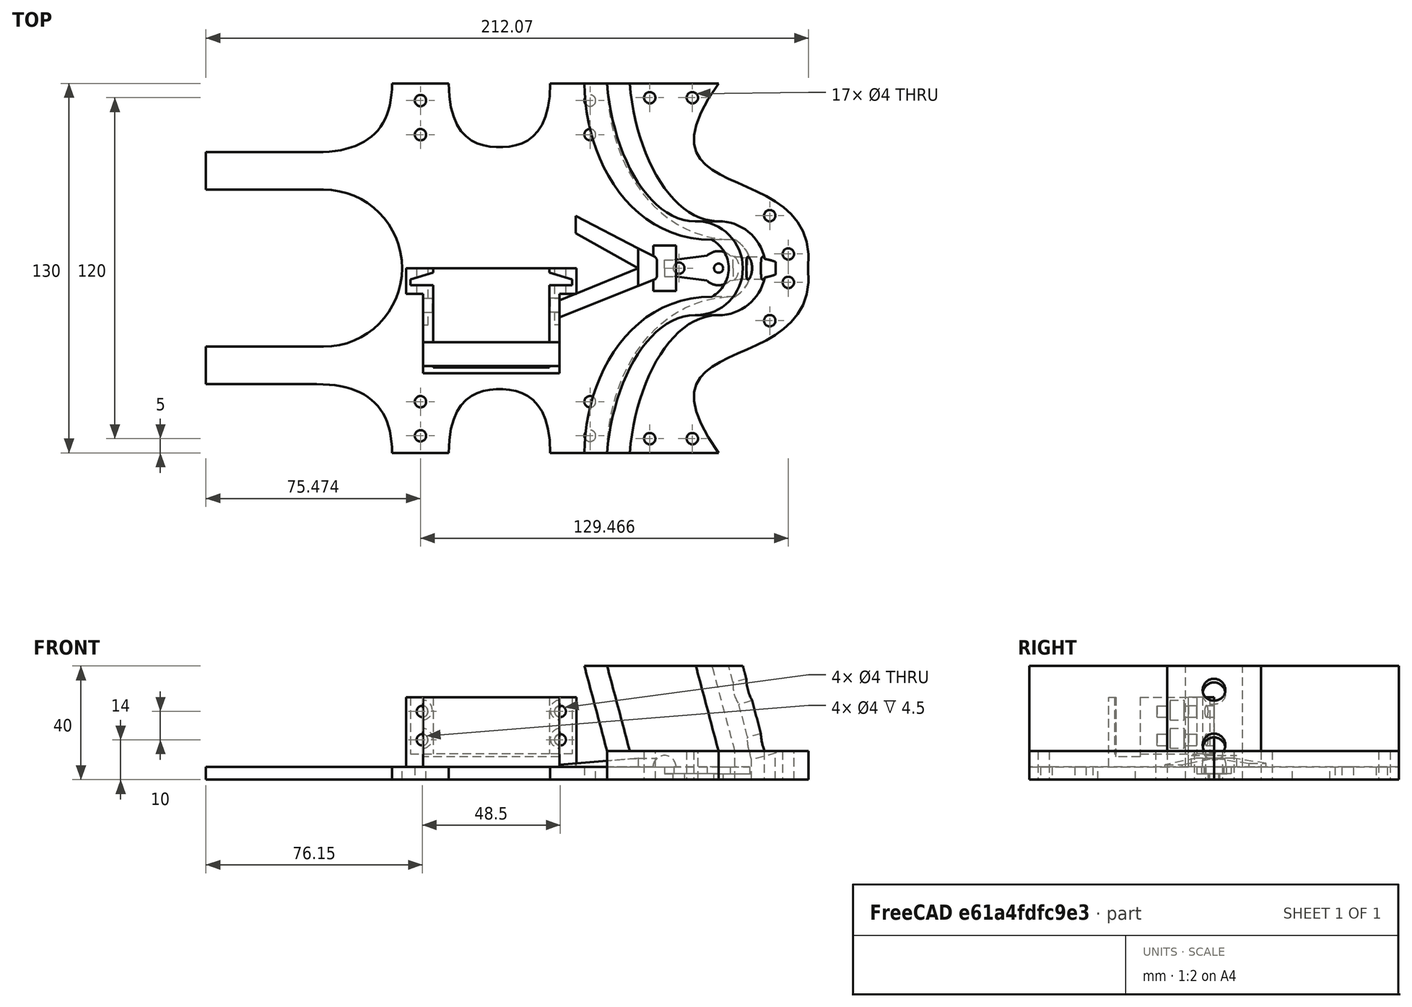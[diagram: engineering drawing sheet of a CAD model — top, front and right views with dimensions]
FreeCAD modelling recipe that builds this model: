
FCSTD DOCUMENT  (FreeCAD 0.18.4R)
Label: Crawler_bottom_2
License: All rights reserved
LicenseURL: http://en.wikipedia.org/wiki/All_rights_reserved
objects: TechDraw::DrawViewDimension×25, Sketcher::SketchObject×17, Part::Extrusion×6, PartDesign::Pocket×6, TechDraw::DrawViewPart×6, PartDesign::FeatureBase×3, PartDesign::Body×3, Part::Mirroring×3, Part::MultiFuse×3, Part::Fuse×3, Part::Cut×2, TechDraw::DrawSVGTemplate×2, TechDraw::DrawViewAnnotation×2, TechDraw::DrawPage×2, Spreadsheet::Sheet×1, PartDesign::Pad×1, Part::Loft×1
note: 55 computed .brp shape members not serialized (recipe doc carries the construction recipe); baked Part::Feature solids carry a one-line shape summary decoded from their .brp

FEATURE [Sketcher::SketchObject] Sketch
  expr: Constraints[11] = Constraints.dv
  expr: Constraints[5] = Constraints.dv
  expr: Constraints[10] = Constraints.dv
  expr: Constraints[4] = Constraints.dh
  expr: Constraints[3] = Constraints.diameterHole
  sketch-geometry (4):
    g0: Circle CenterX=-33 CenterY=5 CenterZ=0 NormalX=0 NormalY=0 NormalZ=1 AngleXU=0 Radius=4
    g1: Circle CenterX=-33 CenterY=-5 CenterZ=0 NormalX=0 NormalY=0 NormalZ=1 AngleXU=0 Radius=4
    g2: Circle CenterX=15 CenterY=5 CenterZ=0 NormalX=0 NormalY=0 NormalZ=1 AngleXU=0 Radius=4
    g3: Circle CenterX=15 CenterY=-5 CenterZ=0 NormalX=0 NormalY=0 NormalZ=1 AngleXU=0 Radius=4
  constraints (12):
    c: DistanceY(g-1,g0) = 5  'dv'
    c: Radius(g0) = 4  'diameterHole'
    c: DistanceX(g0,g-1) = 33  'dh'
    c: Radius(g1) = 4
    c: DistanceX(g1,g-1) = 33
    c: DistanceY(g1,g-1) = 5
    c: Equal(g0,g2) = 4  'diameterHole'
    c: Equal(g1,g3) = 4
    c: DistanceX(g-1,g2) = 15
    c: DistanceX(g-1,g3) = 15
    c: DistanceY(g3,g-1) = 5
    c: DistanceY(g-1,g2) = 5
FEATURE [Sketcher::SketchObject] Sketch001
  sketch-geometry (51):
    g0: GeomPoint X=-180.398 Y=40.8191 Z=0
    g1: LineSegment StartX=-180.398 StartY=40.8191 StartZ=0 EndX=-141.416 EndY=40.8191 EndZ=0
    g2: ArcOfCircle CenterX=0 CenterY=0 CenterZ=0 NormalX=0 NormalY=0 NormalZ=1 AngleXU=0 Radius=11.54 StartAngle=0 EndAngle=1.04825
    g3: ArcOfCircle CenterX=0 CenterY=0 CenterZ=0 NormalX=0 NormalY=0 NormalZ=1 AngleXU=0 Radius=1.6 StartAngle=0 EndAngle=3.14159
    g4: LineSegment StartX=1.6 StartY=0 StartZ=0 EndX=11.54 EndY=0 EndZ=0
    g5: LineSegment StartX=-1.6 StartY=2e-16 StartZ=0 EndX=-111.4 EndY=0 EndZ=0
    g6: ArcOfCircle CenterX=-139.032 CenterY=0 CenterZ=0 NormalX=0 NormalY=0 NormalZ=1 AngleXU=0 Radius=27.6319 StartAngle=0 EndAngle=1.5708
    g7: LineSegment StartX=-139.032 StartY=27.6319 StartZ=0 EndX=-180.398 EndY=27.6319 EndZ=0
    g8: LineSegment StartX=-180.398 StartY=27.6319 StartZ=0 EndX=-180.398 EndY=40.8191 EndZ=0
    g9: LineSegment [constr] StartX=-139.032 StartY=27.6319 StartZ=0 EndX=-139.032 EndY=0 EndZ=0
    g10: Circle [constr] CenterX=-141.416 CenterY=40.8191 CenterZ=0 NormalX=0 NormalY=0 NormalZ=1 AngleXU=0 Radius=2
    g11: Circle [constr] CenterX=-114.926 CenterY=40.8191 CenterZ=0 NormalX=0 NormalY=0 NormalZ=1 AngleXU=0 Radius=2
    g12: Circle [constr] CenterX=-114.926 CenterY=65 CenterZ=0 NormalX=0 NormalY=0 NormalZ=1 AngleXU=0 Radius=2
    g13: BSplineCurve PolesCount=3 KnotsCount=2 Degree=2 IsPeriodic=0
    g14: GeomPoint [constr] X=-141.416 Y=40.8191 Z=0
    g15: GeomPoint [constr] X=-114.926 Y=65 Z=0
    g16: LineSegment StartX=-114.926 StartY=65 StartZ=0 EndX=-94.9256 EndY=65 EndZ=0
    g17-g21: Circle [constr] x5 (B-spline internal-alignment scaffolding for g22; pole/knot coordinates omitted)
    g22: BSplineCurve PolesCount=5 KnotsCount=3 Degree=3 IsPeriodic=0
    g23: GeomPoint [constr] X=-94.9256 Y=65 Z=0
    g24: GeomPoint [constr] X=-77.0831 Y=42.5915 Z=0
    g25: GeomPoint [constr] X=-59.2405 Y=65 Z=0
    g26: LineSegment StartX=-59.2405 StartY=65 StartZ=0 EndX=-39.2405 EndY=65 EndZ=0
    g27-g30: Circle [constr] x4 (B-spline internal-alignment scaffolding for g31; pole/knot coordinates omitted)
    g31: BSplineCurve PolesCount=4 KnotsCount=2 Degree=3 IsPeriodic=0
    g32: GeomPoint [constr] X=-39.2405 Y=65 Z=0
    g33: GeomPoint [constr] X=5.75948 Y=10 Z=0
    g34: LineSegment [constr] StartX=-94.9256 StartY=46.3979 StartZ=0 EndX=-59.2405 EndY=46.3979 EndZ=0
    g35: LineSegment [constr] StartX=-94.9256 StartY=46.3979 StartZ=0 EndX=-77.0831 EndY=38.7852 EndZ=0
    g36: LineSegment [constr] StartX=-77.0831 StartY=38.7852 StartZ=0 EndX=-59.2405 EndY=46.3979 EndZ=0
    g37: LineSegment [constr] StartX=-141.416 StartY=40.8191 StartZ=0 EndX=-114.926 EndY=40.8191 EndZ=0
    g38: LineSegment [constr] StartX=-39.2405 StartY=65 StartZ=0 EndX=-39.2405 EndY=40 EndZ=0
    g39: LineSegment [constr] StartX=-39.2405 StartY=40 StartZ=0 EndX=-39.2405 EndY=10 EndZ=0
    g40: LineSegment [constr] StartX=-39.2405 StartY=10 StartZ=0 EndX=-24.2405 EndY=10 EndZ=0
    g41: LineSegment [constr] StartX=-59.2405 StartY=46.3979 StartZ=0 EndX=-59.2405 EndY=65 EndZ=0
    g42: LineSegment [constr] StartX=5.75948 StartY=10 StartZ=0 EndX=-24.2405 EndY=10 EndZ=0
    g43: LineSegment [constr] StartX=-114.926 StartY=40.8191 StartZ=0 EndX=-114.926 EndY=65 EndZ=0
    g44: LineSegment [constr] StartX=-94.9256 StartY=65 StartZ=0 EndX=-94.9256 EndY=46.3979 EndZ=0
    g45: Circle CenterX=-45.2405 CenterY=59 CenterZ=0 NormalX=0 NormalY=0 NormalZ=1 AngleXU=0 Radius=2
    g46: Circle CenterX=-45.2405 CenterY=47 CenterZ=0 NormalX=0 NormalY=0 NormalZ=1 AngleXU=0 Radius=2
    g47: LineSegment [constr] StartX=-45.2405 StartY=59 StartZ=0 EndX=-45.2405 EndY=47 EndZ=0
    g48: Circle CenterX=-104.926 CenterY=59 CenterZ=0 NormalX=0 NormalY=0 NormalZ=1 AngleXU=0 Radius=2
    g49: Circle CenterX=-104.926 CenterY=47 CenterZ=0 NormalX=0 NormalY=0 NormalZ=1 AngleXU=0 Radius=2
    g50: LineSegment [constr] StartX=-104.926 StartY=59 StartZ=0 EndX=-104.926 EndY=47 EndZ=0
  constraints (106):
    c: Coincident(g1,g0)
    c: Horizontal(g1)
    c: Coincident(g2,g-1)
    c: PointOnObject(g2,g-1)
    c: PointOnObject(g5,g-1)
    c: Coincident(g3,g-1)
    c: PointOnObject(g3,g-1)
    c: Coincident(g4,g3)
    c: Coincident(g4,g2)
    c: Horizontal(g4)
    c: Coincident(g5,g3)
    c: Radius(g3) = 1.6
    c: PointOnObject(g6,g-1)
    c: Coincident(g6,g5)
    c: Coincident(g7,g6)
    c: Horizontal(g7)
    c: Coincident(g8,g7)
    c: Vertical(g8)
    c: Coincident(g8,g0)
    c: Coincident(g9,g6)
    c: Vertical(g9)
    c: Coincident(g6,g9)
    c: Coincident(g13,g1)
    c: Radius(g10) = 2
    c: Equal(g10,g11)
    c: Equal(g10,g12)
    c: InternalAlignment(g10,g13)
    c: InternalAlignment(g11,g13)
    c: InternalAlignment(g12,g13)
    c: InternalAlignment(g14,g13)
    c: InternalAlignment(g15,g13)
    c: Coincident(g16,g13)
    c: Horizontal(g16)
    c: Coincident(g22,g16)
    c: Radius(g17) = 3
    c: Equal(g17, g18-g21) x4
    c: InternalAlignment(g17-g21 -> g22) x5
    c: InternalAlignment(g23,g22)
    c: InternalAlignment(g24,g22)
    c: InternalAlignment(g25,g22)
    c: Coincident(g26,g22)
    c: Horizontal(g26)
    c: Coincident(g31,g26)
    c: Radius(g27) = 5
    c: Equal(g27,g28)
    c: Equal(g27,g29)
    c: Equal(g27,g30)
    c: InternalAlignment(g27-g30 -> g31) x4
    c: InternalAlignment(g32,g31)
    c: InternalAlignment(g33,g31)
    c: Coincident(g34,g18)
    c: Coincident(g34,g20)
    c: Horizontal(g34)
    c: Coincident(g35,g18)
    c: Coincident(g35,g19)
    c: Coincident(g36,g20)
    c: Equal(g36,g35)
    c: Coincident(g19,g36)
    c: Coincident(g37,g1)
    c: Coincident(g37,g11)
    c: Horizontal(g37)
    c: Coincident(g38,g26)
    c: Coincident(g38,g28)
    c: Vertical(g38)
    c: Coincident(g39,g28)
    c: Vertical(g39)
    c: Coincident(g40,g39)
    c: Coincident(g40,g29)
    c: Horizontal(g40)
    c: DistanceY(g38,g38) = 25
    c: Coincident(g41,g20)
    c: Coincident(g41,g22)
    c: Vertical(g41)
    c: DistanceY(g39,g39) = 30
    c: Coincident(g42,g29)
    c: Horizontal(g42)
    c: DistanceX(g40,g40) = 15
    c: DistanceX(g42,g42) = 30
    c: Coincident(g43,g11)
    c: Coincident(g43,g13)
    c: Vertical(g43)
    c: Coincident(g44,g16)
    c: Coincident(g44,g18)
    c: Vertical(g44)
    c: Radius(g45) = 2
    c: Equal(g45,g46) = 2
    c: Coincident(g47,g45)
    c: Coincident(g47,g46)
    c: Vertical(g47)
    c: DistanceX(g26,g26) = 20
    c: DistanceX(g22,g45) = 14
    c: DistanceY(g45,g22) = 6
    c: DistanceY(g47,g47) = 12
    c: DistanceY(g2,g26) = 65
    c: Equal(g45,g48) = 2
    c: Equal(g48,g49) = 2
    c: Coincident(g50,g48)
    c: Coincident(g50,g49)
    c: Vertical(g50)
    c: Equal(g47,g50) = 12
    c: DistanceX(g16,g16) = 20
    c: DistanceX(g13,g48) = 10
    c: DistanceY(g48,g13) = 6
    c: DistanceY(g2,g16) = 65
    c: DistanceX(g2,g2) = 11.54
    c: DistanceY(g2,g2) = 10
FEATURE [Part::Extrusion] Extrude  label="arm"
  Base = -> Sketch001
  Dir = (0,0,1)
  DirMode = 2
  FaceMakerClass = Part::FaceMakerBullseye
  LengthFwd = 4.5
  LengthRev = 0
  Solid = true
  Symmetric = false
  expr: LengthFwd = global.height
FEATURE [Sketcher::SketchObject] Sketch003  label="ExtrudeToLayOn"
  AttachmentOffset = pos=(0,0,0) rot=(0,0,1;1.5708rad)
  MapMode = 2
  Placement = pos=(0,0,0) rot=(0,0,1;1.5708rad)
  Support = -> [Sketch001]
  expr: Constraints.length = Constraints.hi
  sketch-geometry (10):
    g0: LineSegment StartX=0 StartY=110 StartZ=0 EndX=0 EndY=50 EndZ=0
    g1: LineSegment StartX=-37 StartY=56 StartZ=0 EndX=-37 EndY=104 EndZ=0
    g2: LineSegment StartX=-37 StartY=104 StartZ=0 EndX=-9 EndY=104 EndZ=0
    g3: LineSegment StartX=-37 StartY=56 StartZ=0 EndX=-9 EndY=56 EndZ=0
    g4: LineSegment StartX=0 StartY=50 StartZ=0 EndX=-9 EndY=50 EndZ=0
    g5: LineSegment StartX=-9 StartY=50 StartZ=0 EndX=-9 EndY=56 EndZ=0
    g6: LineSegment StartX=0 StartY=110 StartZ=0 EndX=-9 EndY=110 EndZ=0
    g7: LineSegment StartX=-9 StartY=104 StartZ=0 EndX=-9 EndY=110 EndZ=0
    g8: LineSegment [constr] StartX=-9 StartY=104 StartZ=0 EndX=-9 EndY=80 EndZ=0
    g9: LineSegment [constr] StartX=-9 StartY=80 StartZ=0 EndX=-9 EndY=56 EndZ=0
  constraints (29):
    c: Vertical(g0)
    c: Vertical(g1)
    c: DistanceY(g0,g0) = 60
    c: Coincident(g2,g1)
    c: Horizontal(g2)
    c: DistanceX(g2,g2) = 28  'hi'
    c: Coincident(g3,g1)
    c: Horizontal(g3)
    c: DistanceX(g3,g3) = 28  'length'
    c: Coincident(g4,g0)
    c: Horizontal(g4)
    c: Coincident(g5,g4)
    c: Coincident(g5,g3)
    c: Vertical(g5)
    c: Coincident(g6,g0)
    c: Horizontal(g6)
    c: Vertical(g7)
    c: Coincident(g7,g6)
    c: Coincident(g2,g7)
    c: Equal(g5,g7)
    c: DistanceY(g1,g1) = 48
    c: DistanceX(g4,g0) = 9
    c: DistanceX(g1,g-1) = 37
    c: Coincident(g8,g2)
    c: Vertical(g8)
    c: Coincident(g9,g8)
    c: Coincident(g9,g3)
    c: Equal(g8,g9)
    c: DistanceY(g-1,g8) = 80
FEATURE [Part::Extrusion] Extrude001
  Base = -> Sketch003
  Dir = (0,0,1)
  DirMode = 2
  FaceMakerClass = Part::FaceMakerBullseye
  LengthFwd = 25
  LengthRev = 0
  Placement = pos=(0,0,2) rot=(0,0,1;0rad)
  Solid = true
  Symmetric = false
FEATURE [Sketcher::SketchObject] Sketch004  label="Servo"
  AttachmentOffset = pos=(0,-3,-2) rot=(0,0,1;0rad)
  MapMode = 5
  Placement = pos=(0,-3,25) rot=(0,0,1;0rad)
  Support = -> [Extrude001]
  expr: Constraints[35] = Constraints.strebeH
  sketch-geometry (21):
    g0: LineSegment StartX=-100.5 StartY=4.5 StartZ=0 EndX=-59.5 EndY=4.5 EndZ=0
    g1: LineSegment StartX=-59.5 StartY=-32 StartZ=0 EndX=-100.5 EndY=-32 EndZ=0
    g2: LineSegment [constr] StartX=-59.5 StartY=4.5 StartZ=0 EndX=-59.5 EndY=-1 EndZ=0
    g3: LineSegment [constr] StartX=-59.5 StartY=-1 StartZ=0 EndX=-51.5 EndY=-1 EndZ=0
    g4: LineSegment StartX=-51.5 StartY=-1 StartZ=0 EndX=-51.5 EndY=-3 EndZ=0
    g5: LineSegment StartX=-51.5 StartY=-3 StartZ=0 EndX=-59.5 EndY=-3 EndZ=0
    g6: LineSegment [constr] StartX=-100.5 StartY=4.5 StartZ=0 EndX=-100.5 EndY=-1 EndZ=0
    g7: LineSegment [constr] StartX=-100.5 StartY=-1 StartZ=0 EndX=-108.5 EndY=-1 EndZ=0
    g8: LineSegment StartX=-108.5 StartY=-1 StartZ=0 EndX=-108.5 EndY=-3 EndZ=0
    g9: LineSegment StartX=-108.5 StartY=-3 StartZ=0 EndX=-100.5 EndY=-3 EndZ=0
    g10: GeomPoint X=-80 Y=-3 Z=0
    g11: LineSegment [constr] StartX=-100.5 StartY=-3 StartZ=0 EndX=-80 EndY=-3 EndZ=0
    g12: LineSegment [constr] StartX=-80 StartY=-3 StartZ=0 EndX=-59.5 EndY=-3 EndZ=0
    g13: GeomPoint X=-59.5 Y=1.5 Z=0
    g14: GeomPoint X=-100.5 Y=1.5 Z=0
    g15: LineSegment StartX=-108.5 StartY=-1 StartZ=0 EndX=-100.5 EndY=1.5 EndZ=0
    g16: LineSegment StartX=-100.5 StartY=1.5 StartZ=0 EndX=-100.5 EndY=4.5 EndZ=0
    g17: LineSegment StartX=-51.5 StartY=-1 StartZ=0 EndX=-59.5 EndY=1.5 EndZ=0
    g18: LineSegment StartX=-59.5 StartY=1.5 StartZ=0 EndX=-59.5 EndY=4.5 EndZ=0
    g19: LineSegment StartX=-100.5 StartY=-3 StartZ=0 EndX=-100.5 EndY=-32 EndZ=0
    g20: LineSegment StartX=-59.5 StartY=-32 StartZ=0 EndX=-59.5 EndY=-3 EndZ=0
  constraints (54):
    c: Horizontal(g0)
    c: DistanceX(g0,g0) = 41  'vl'
    c: DistanceY(g1,g0) = 36.5
    c: Coincident(g2,g0)
    c: Vertical(g2)
    c: DistanceY(g2,g2) = 5.5  'vh'
    c: Coincident(g3,g2)
    c: Horizontal(g3)
    c: Coincident(g4,g3)
    c: Vertical(g4)
    c: Coincident(g5,g4)
    c: Horizontal(g5)
    c: DistanceX(g0,g1) = 0
    c: Vertical(g6)
    c: Coincident(g7,g6)
    c: Horizontal(g7)
    c: Coincident(g8,g7)
    c: Vertical(g8)
    c: Coincident(g9,g8)
    c: Horizontal(g9)
    c: Coincident(g6,g0)
    c: DistanceY(g6,g6) = 5.5
    c: DistanceY(g1,g9) = 29
    c: Horizontal(g1)
    c: DistanceX(g1,g1) = 41
    c: DistanceX(g7,g6) = 8
    c: DistanceX(g2,g3) = 8
    c: Coincident(g11,g10)
    c: Horizontal(g11)
    c: Coincident(g12,g10)
    c: Equal(g11,g12)
    c: DistanceX(g10,g-1) = 80  'HvonOrg'
    c: PointOnObject(g13,g2)
    c: DistanceY(g2,g13) = 2.5  'strebeH'
    c: PointOnObject(g14,g6)
    c: DistanceY(g6,g14) = 2.5
    c: Coincident(g15,g7)
    c: Coincident(g15,g14)
    c: Coincident(g16,g14)
    c: Coincident(g16,g0)
    c: Coincident(g17,g3)
    c: Coincident(g17,g13)
    c: Coincident(g18,g13)
    c: Coincident(g18,g0)
    c: Coincident(g19,g9)
    c: Coincident(g19,g1)
    c: Vertical(g19)
    c: Coincident(g20,g1)
    c: Vertical(g20)
    c: Coincident(g5,g20)
    c: Coincident(g5,g12)
    c: Coincident(g9,g11)
    c: Horizontal(g12)
    c: DistanceY(g1,g-1) = 32
FEATURE [PartDesign::FeatureBase] BaseFeature001
  BaseFeature = -> Extrude001
FEATURE [PartDesign::Pocket] Pocket001
  BaseFeature = -> BaseFeature001
  Length = 20
  Length2 = 100
  Profile = -> Sketch004
  Type = 0
FEATURE [Sketcher::SketchObject] Sketch005  label="ServoHoles"
  MapMode = 5
  Placement = pos=(0,2e-16,0) rot=(0,0.707107,0.707107;3.14159rad)
  Support = -> [Pocket001]
  expr: Constraints.height = 5mm + 5mm
  expr: Constraints[14] = Sketch004.Constraints.HvonOrg
  sketch-geometry (7):
    g0: Circle CenterX=55.75 CenterY=20 CenterZ=0 NormalX=0 NormalY=0 NormalZ=1 AngleXU=0 Radius=2
    g1: Circle CenterX=55.75 CenterY=10 CenterZ=0 NormalX=0 NormalY=0 NormalZ=1 AngleXU=0 Radius=2
    g2: Circle CenterX=104.25 CenterY=10 CenterZ=0 NormalX=0 NormalY=0 NormalZ=1 AngleXU=0 Radius=2
    g3: Circle CenterX=104.25 CenterY=20 CenterZ=0 NormalX=0 NormalY=0 NormalZ=1 AngleXU=0 Radius=2
    g4: GeomPoint X=57.75 Y=20 Z=0
    g5: GeomPoint X=102.25 Y=20 Z=0
    g6: GeomPoint X=80 Y=8 Z=0
  constraints (17):
    c: Radius(g0) = 2  'rad'
    c: Equal(g0,g1) = 2  'rad'
    c: DistanceY(g1,g0) = 10
    c: DistanceX(g0,g1) = 0
    c: Equal(g0,g3) = 2  'rad'
    c: Equal(g3,g2) = 2  'rad'
    c: DistanceY(g2,g3) = 10
    c: DistanceX(g3,g2) = 0
    c: DistanceY(g0,g3) = 0
    c: DistanceY(g-1,g1) = 10  'height'
    c: PointOnObject(g4,g0)
    c: PointOnObject(g5,g3)
    c: DistanceY(g4,g0) = 0
    c: DistanceY(g5,g4) = 0
    c: DistanceX(g-1,g6) = 80
    c: DistanceX(g4,g6) = 22.25
    c: DistanceX(g6,g5) = 22.25
FEATURE [PartDesign::Pocket] Pocket002
  BaseFeature = -> Pocket001
  Length = 20
  Length2 = 100
  Profile = -> Sketch005
  Type = 0
FEATURE [PartDesign::Body] Body001
  BaseFeature = -> Extrude001
  Group = -> [BaseFeature001,Sketch004,Pocket001,Sketch005,Pocket002]
  Origin = -> Origin001
  Placement = pos=(0,0,4) rot=(0,0,1;0rad)
  Tip = -> Pocket002
  expr: Placement.Base.y = global.offestSev
FEATURE [Sketcher::SketchObject] Sketch007
  Placement = pos=(2,0,17) rot=(0,0,1;1.5708rad)
  expr: Constraints[28] = Constraints.vh
  expr: Constraints[29] = Constraints.vh2
  sketch-geometry (12):
    g0: LineSegment StartX=1.28047 StartY=41.4016 StartZ=0 EndX=42.2805 EndY=41.4016 EndZ=0
    g1: LineSegment StartX=42.2805 StartY=4.90163 StartZ=0 EndX=1.04145 EndY=4.90163 EndZ=0
    g2: LineSegment StartX=42.2805 StartY=4.90163 StartZ=0 EndX=42.2805 EndY=31.3016 EndZ=0
    g3: LineSegment StartX=42.2805 StartY=41.4016 StartZ=0 EndX=42.2805 EndY=35.4016 EndZ=0
    g4: LineSegment StartX=42.2805 StartY=35.4016 StartZ=0 EndX=48.9967 EndY=35.4016 EndZ=0
    g5: LineSegment StartX=48.9967 StartY=35.4016 StartZ=0 EndX=48.9967 EndY=31.3016 EndZ=0
    g6: LineSegment StartX=48.9967 StartY=31.3016 StartZ=0 EndX=42.2805 EndY=31.3016 EndZ=0
    g7: LineSegment StartX=1.04145 StartY=4.90163 StartZ=0 EndX=1.04145 EndY=31.3016 EndZ=0
    g8: LineSegment StartX=1.28047 StartY=41.4016 StartZ=0 EndX=1.28047 EndY=35.4016 EndZ=0
    g9: LineSegment StartX=1.28047 StartY=35.4016 StartZ=0 EndX=-5.63119 EndY=35.4016 EndZ=0
    g10: LineSegment StartX=-5.63119 StartY=35.4016 StartZ=0 EndX=-5.63119 EndY=31.3016 EndZ=0
    g11: LineSegment StartX=-5.63119 StartY=31.3016 StartZ=0 EndX=1.04145 EndY=31.3016 EndZ=0
  constraints (31):
    c: Horizontal(g0)
    c: DistanceX(g0,g0) = 41  'v'
    c: DistanceY(g1,g0) = 36.5
    c: Coincident(g2,g1)
    c: Vertical(g2)
    c: DistanceY(g2,g2) = 26.4  'vh2'
    c: Coincident(g3,g0)
    c: Vertical(g3)
    c: DistanceY(g3,g3) = 6  'vh'
    c: Coincident(g4,g3)
    c: Horizontal(g4)
    c: Coincident(g5,g4)
    c: Vertical(g5)
    c: Coincident(g6,g5)
    c: Coincident(g6,g2)
    c: Horizontal(g6)
    c: DistanceX(g0,g1) = 0
    c: Vertical(g7)
    c: Vertical(g8)
    c: Coincident(g9,g8)
    c: Horizontal(g9)
    c: Coincident(g10,g9)
    c: Vertical(g10)
    c: Coincident(g11,g10)
    c: Coincident(g11,g7)
    c: Horizontal(g11)
    c: Coincident(g8,g0)
    c: Coincident(g1,g7)
    c: DistanceY(g8,g8) = 6
    c: DistanceY(g7,g7) = 26.4
    c: Horizontal(g1)
FEATURE [Sketcher::SketchObject] Sketch008  label="ServoHole"
  AttachmentOffset = pos=(0,0,4.5) rot=(0,0,1;0rad)
  Placement = pos=(0,0,4.5) rot=(0,0,1;1.5708rad)
  expr: AttachmentOffset.Base.z = global.height
  sketch-geometry (7):
    g0: GeomPoint X=0 Y=19 Z=0
    g1: LineSegment StartX=0 StartY=19 StartZ=0 EndX=2.9 EndY=19 EndZ=0
    g2: LineSegment StartX=2.9 StartY=19 StartZ=0 EndX=2.9 EndY=15.6827 EndZ=0
    g3: ArcOfCircle CenterX=0 CenterY=0 CenterZ=0 NormalX=0 NormalY=0 NormalZ=1 AngleXU=0 Radius=6 StartAngle=0 EndAngle=0.747584
    g4: LineSegment StartX=4.4 StartY=4.07922 StartZ=0 EndX=2.9 EndY=15.6827 EndZ=0
    g5: LineSegment StartX=0 StartY=0 StartZ=0 EndX=6 EndY=0 EndZ=0
    g6: LineSegment StartX=0 StartY=0 StartZ=0 EndX=0 EndY=19 EndZ=0
  constraints (18):
    c: PointOnObject(g0,g-2)
    c: DistanceY(g-1,g0) = 19  'servHoleL'
    c: Coincident(g1,g0)
    c: Horizontal(g1)
    c: DistanceX(g1,g1) = 2.9
    c: Coincident(g2,g1)
    c: Vertical(g2)
    c: Coincident(g3,g-1)
    c: Radius(g3) = 6
    c: PointOnObject(g3,g-1)
    c: DistanceX(g-1,g3) = 4.4
    c: Coincident(g4,g2)
    c: Distance(g4) = 11.7
    c: Coincident(g4,g3)
    c: Coincident(g5,g-1)
    c: Coincident(g5,g3)
    c: Coincident(g6,g-1)
    c: Coincident(g6,g0)
FEATURE [Spreadsheet::Sheet] Spreadsheet  label="global"
  cells = A1=height; B1(height)=4.5; A2=offsetBackwardServo; B2(offestSev)=0
FEATURE [Part::Extrusion] Extrude004
  Base = -> Sketch008
  Dir = (0,0,1)
  DirMode = 2
  FaceMakerClass = Part::FaceMakerBullseye
  LengthFwd = 2.45
  LengthRev = 0
  Reversed = true
  Solid = true
  Symmetric = false
FEATURE [Part::Mirroring] Part__Mirroring002  label="Extrude004 (Mirror #3)"
  Base = (0,0,0)
  Normal = (1,0,0)
  Source = -> Extrude004
FEATURE [Part::MultiFuse] Fusion003
  Shapes = -> [Part__Mirroring002,Extrude004]
FEATURE [Part::Cut] Cut
  Base = -> Extrude
  Tool = -> Fusion003
FEATURE [Part::Mirroring] Part__Mirroring  label="Extrude (Mirror #1)"
  Base = (0,0,0)
  Normal = (0,1,0)
  Source = -> Cut
FEATURE [Sketcher::SketchObject] Sketch009  label="servoScrewSmallWhole"
  Placement = pos=(0,0,4.5) rot=(0,0,1;0rad)
  expr: Placement.Base.z = global.height
  sketch-geometry (3):
    g0: GeomPoint X=-19 Y=0 Z=0
    g1: GeomPoint X=-14 Y=0 Z=0
    g2: Circle CenterX=-14 CenterY=0 CenterZ=0 NormalX=0 NormalY=0 NormalZ=1 AngleXU=0 Radius=2
  constraints (5):
    c: PointOnObject(g0,g-1)
    c: DistanceX(g0,g-1) = 19
    c: PointOnObject(g1,g-1)
    c: DistanceX(g0,g1) = 5
    c: Radius(g2) = 2
FEATURE [Sketcher::SketchObject] Sketch010  label="ServoHoles001"
  AttachmentOffset = pos=(0,0,-10.5) rot=(0,0,1;0rad)
  MapMode = 5
  Placement = pos=(-2.3e-15,-10.5,2.3e-15) rot=(0,0.707107,0.707107;3.14159rad)
  Support = -> [Pocket001]
  expr: Constraints.height = 5mm + 5mm + 4.5mm
  expr: Constraints[16] = Constraints.widthDist
  expr: Constraints[14] = Sketch004.Constraints.HvonOrg
  sketch-geometry (7):
    g0: Circle CenterX=55.75 CenterY=24.5 CenterZ=0 NormalX=0 NormalY=0 NormalZ=1 AngleXU=0 Radius=3.5
    g1: Circle CenterX=55.75 CenterY=14.5 CenterZ=0 NormalX=0 NormalY=0 NormalZ=1 AngleXU=0 Radius=3.5
    g2: Circle CenterX=104.25 CenterY=14.5 CenterZ=0 NormalX=0 NormalY=0 NormalZ=1 AngleXU=0 Radius=3.5
    g3: Circle CenterX=104.25 CenterY=24.5 CenterZ=0 NormalX=0 NormalY=0 NormalZ=1 AngleXU=0 Radius=3.5
    g4: GeomPoint X=59.25 Y=24.5 Z=0
    g5: GeomPoint X=100.75 Y=24.5 Z=0
    g6: GeomPoint X=80 Y=8 Z=0
  constraints (17):
    c: Radius(g0) = 3.5  'rad'
    c: Equal(g0,g1) = 2  'rad'
    c: DistanceY(g1,g0) = 10
    c: DistanceX(g0,g1) = 0
    c: Equal(g0,g3) = 2  'rad'
    c: Equal(g3,g2) = 2  'rad'
    c: DistanceY(g2,g3) = 10
    c: DistanceX(g3,g2) = 0
    c: DistanceY(g0,g3) = 0
    c: DistanceY(g-1,g1) = 14.5  'height'
    c: PointOnObject(g4,g0)
    c: PointOnObject(g5,g3)
    c: DistanceY(g4,g0) = 0
    c: DistanceY(g5,g4) = 0
    c: DistanceX(g-1,g6) = 80
    c: DistanceX(g4,g6) = 20.75  'widthDist'
    c: DistanceX(g6,g5) = 20.75
FEATURE [Sketcher::SketchObject] Sketch011  label="CableHole"
  MapMode = 5
  Placement = pos=(-56,1.23e-14,0) rot=(0.57735,0.57735,0.57735;2.0944rad)
  Support = -> [Pocket002]
  sketch-geometry (5):
    g0: GeomPoint X=-5 Y=4 Z=0
    g1: LineSegment StartX=-34.5 StartY=37.056 StartZ=0 EndX=-26 EndY=37.056 EndZ=0
    g2: LineSegment StartX=-26 StartY=37.056 StartZ=0 EndX=-26 EndY=8 EndZ=0
    g3: LineSegment StartX=-26 StartY=8 StartZ=0 EndX=-34.5 EndY=8 EndZ=0
    g4: LineSegment StartX=-34.5 StartY=8 StartZ=0 EndX=-34.5 EndY=37.056 EndZ=0
  constraints (13):
    c: DistanceX(g-1,g0) = -5
    c: Coincident(g1,g2)
    c: Coincident(g2,g3)
    c: Coincident(g3,g4)
    c: Coincident(g4,g1)
    c: Horizontal(g1)
    c: Horizontal(g3)
    c: Vertical(g2)
    c: Vertical(g4)
    c: DistanceX(g2,g0) = 21
    c: DistanceX(g3,g3) = 8.5
    c: DistanceY(g-1,g0) = 4
    c: DistanceY(g0,g2) = 4
FEATURE [Sketcher::SketchObject] Sketch013
  MapMode = 5
  Placement = pos=(0,0,0) rot=(1,0,0;1.5708rad)
  sketch-geometry (3):
    g0: LineSegment StartX=-59 StartY=5 StartZ=0 EndX=-22.1184 EndY=8 EndZ=0
    g1: LineSegment StartX=-22.1184 StartY=8 StartZ=0 EndX=-59 EndY=8 EndZ=0
    g2: LineSegment StartX=-59 StartY=8 StartZ=0 EndX=-59 EndY=5 EndZ=0
  constraints (8):
    c: Coincident(g1,g0)
    c: Horizontal(g1)
    c: Coincident(g2,g1)
    c: Coincident(g2,g0)
    c: Vertical(g2)
    c: DistanceX(g0,g-1) = 59
    c: DistanceY(g-1,g0) = 8
    c: DistanceY(g0,g1) = 3
FEATURE [Part::Extrusion] Extrude006
  Base = -> Sketch013
  Dir = (0,-1,2e-16)
  DirMode = 2
  FaceMakerClass = Part::FaceMakerBullseye
  LengthFwd = 30
  LengthRev = 30
  Solid = true
  Symmetric = false
FEATURE [Part::Fuse] Fusion
  Base = -> Cut
  Tool = -> Part__Mirroring
FEATURE [Part::Fuse] Fusion001
  Base = -> Fusion
  Tool = -> Body001
FEATURE [PartDesign::FeatureBase] BaseFeature002
  BaseFeature = -> Fusion001
FEATURE [PartDesign::Pocket] Pocket003
  BaseFeature = -> BaseFeature002
  Length = 10
  Length2 = 100
  Profile = -> Sketch009
  Type = 0
FEATURE [PartDesign::Pocket] Pocket
  BaseFeature = -> Pocket003
  Length = 5
  Length2 = 100
  Profile = -> Sketch010
  Type = 0
FEATURE [PartDesign::Pocket] Pocket004
  BaseFeature = -> Pocket
  Length = 50
  Length2 = 100
  Profile = -> Sketch011
  Type = 0
FEATURE [TechDraw::DrawSVGTemplate] Template
  EditableTexts = Designed_by_Name=Johannes Löwe; Drawing_number=0.0.1; FC-Date=08.08.2021; FC-SC=-; FC-SH=1; FC-Title=RWML Crawler; Subtitle=Base; Weight=19.5 g
  Height = 210
  Orientation = 1
  Width = 297
FEATURE [Sketcher::SketchObject] Sketch014  label="shoe"
  Placement = pos=(0,0,0) rot=(1,0,0;1.5708rad)
  expr: Constraints[6] = global.height
  expr: Constraints[5] = ServoHole.Constraints.servHoleL
  sketch-geometry (2):
    g0: ArcOfCircle CenterX=-19 CenterY=4.5 CenterZ=0 NormalX=0 NormalY=0 NormalZ=1 AngleXU=0 Radius=4 StartAngle=2e-16 EndAngle=3.14159
    g1: LineSegment StartX=-23 StartY=4.5 StartZ=0 EndX=-15 EndY=4.5 EndZ=0
  constraints (7):
    c: Radius(g0) = 4
    c: Coincident(g1,g0)
    c: Coincident(g1,g0)
    c: Horizontal(g1)
    c: PointOnObject(g0,g1)
    c: DistanceX(g0,g-1) = 19
    c: DistanceY(g-1,g0) = 4.5
FEATURE [PartDesign::Pad] Pad
  BaseFeature = -> Pocket004
  Length = 8
  Length2 = 8
  Profile = -> Sketch014
  Type = 4
FEATURE [PartDesign::Body] Body002
  BaseFeature = -> Fusion001
  Group = -> [BaseFeature002,Sketch009,Pocket003,Sketch010,Pocket,Sketch011,Pocket004,Sketch014,Pad]
  Origin = -> Origin002
  Tip = -> Pad
FEATURE [Sketcher::SketchObject] Sketch012  label="V-strong"
  MapMode = 5
  Placement = pos=(0,0,4.5) rot=(0,0,1;0rad)
  Support = -> [Pad]
  sketch-geometry (7):
    g0: LineSegment StartX=-50.2997 StartY=18.3493 StartZ=0 EndX=-22.213 EndY=3.87885 EndZ=0
    g1: LineSegment StartX=-22.213 StartY=-3.87885 StartZ=0 EndX=-56.0787 EndY=-17.3272 EndZ=0
    g2: LineSegment StartX=-56.0787 StartY=-17.3272 StartZ=0 EndX=-56.0787 EndY=-11.3272 EndZ=0
    g3: LineSegment StartX=-56.0787 StartY=-11.3272 StartZ=0 EndX=-28.213 EndY=0 EndZ=0
    g4: LineSegment StartX=-28.213 StartY=0 StartZ=0 EndX=-50.2997 EndY=12.3493 EndZ=0
    g5: LineSegment StartX=-50.2997 StartY=12.3493 StartZ=0 EndX=-50.2997 EndY=18.3493 EndZ=0
    g6: ArcOfCircle CenterX=-28.213 CenterY=0 CenterZ=0 NormalX=0 NormalY=0 NormalZ=1 AngleXU=0 Radius=7.14461 StartAngle=5.70929 EndAngle=6.85708
  constraints (15):
    c: Coincident(g2,g1)
    c: Vertical(g2)
    c: Coincident(g3,g2)
    c: PointOnObject(g3,g-1)
    c: Coincident(g4,g3)
    c: Coincident(g5,g4)
    c: Coincident(g5,g0)
    c: Vertical(g5)
    c: DistanceY(g2,g2) = 6
    c: DistanceY(g5,g5) = 6
    c: Coincident(g6,g3)
    c: Coincident(g6,g0)
    c: Coincident(g6,g1)
    c: DistanceX(g3,g0) = 6
    c: DistanceX(g3,g1) = 6
FEATURE [Part::Extrusion] Extrude005
  Base = -> Sketch012
  Dir = (0,0,1)
  DirMode = 2
  FaceMakerClass = Part::FaceMakerBullseye
  LengthFwd = 3
  LengthRev = 0
  Solid = true
  Symmetric = false
FEATURE [Part::Cut] Cut001
  Base = -> Extrude005
  Tool = -> Extrude006
FEATURE [Part::Fuse] Fusion004
  Base = -> Body002
  Tool = -> Cut001
FEATURE [TechDraw::DrawViewPart] View  label="Top"
  CoarseView = false
  Direction = (0,0,1)
  Focus = 100
  HardHidden = false
  IsoCount = 0
  IsoHidden = false
  IsoVisible = true
  LockPosition = false
  Perspective = false
  Rotation = 0
  Scale = 0.6
  ScaleType = 1
  SeamHidden = false
  SeamVisible = false
  SmoothHidden = false
  SmoothVisible = true
  Source = -> [Fusion004]
  X = 75.929
  Y = 66.9913
FEATURE [TechDraw::DrawViewPart] View001  label="Front"
  CoarseView = false
  Direction = (0,1,0)
  Focus = 100
  HardHidden = false
  IsoCount = 0
  IsoHidden = false
  IsoVisible = false
  LockPosition = false
  Perspective = true
  Rotation = 0
  Scale = 0.6
  ScaleType = 0
  SeamHidden = false
  SeamVisible = false
  SmoothHidden = false
  SmoothVisible = true
  Source = -> [Fusion004]
  X = 203.307
  Y = 80.5986
FEATURE [TechDraw::DrawViewPart] View002  label="Perspective"
  CoarseView = false
  Direction = (-0.2,1,1)
  Focus = 200
  HardHidden = false
  IsoCount = 0
  IsoHidden = false
  IsoVisible = true
  LockPosition = false
  Perspective = false
  Rotation = 0
  Scale = 0.75
  ScaleType = 0
  SeamHidden = false
  SeamVisible = false
  SmoothHidden = true
  SmoothVisible = true
  Source = -> [Fusion004]
  X = 88.4043
  Y = 157.747
  expr: Direction.x = -0.2
FEATURE [Sketcher::SketchObject] Sketch015  label="Resetbuffer"
  sketch-geometry (28):
    g0: ArcOfCircle CenterX=0 CenterY=0 CenterZ=0 NormalX=0 NormalY=0 NormalZ=1 AngleXU=0 Radius=11.54 StartAngle=0 EndAngle=1.04825
    g1-g4: Circle [constr] x4 (B-spline internal-alignment scaffolding for g5; pole/knot coordinates omitted)
    g5: BSplineCurve PolesCount=4 KnotsCount=2 Degree=3 IsPeriodic=0
    g6: GeomPoint [constr] X=-39.2405 Y=65 Z=0
    g7: GeomPoint [constr] X=5.75948 Y=10 Z=0
    g8: LineSegment [constr] StartX=-39.2405 StartY=65 StartZ=0 EndX=-39.2405 EndY=40 EndZ=0
    g9: LineSegment [constr] StartX=-39.2405 StartY=40 StartZ=0 EndX=-39.2405 EndY=10 EndZ=0
    g10: LineSegment [constr] StartX=-39.2405 StartY=10 StartZ=0 EndX=-24.2405 EndY=10 EndZ=0
    g11: LineSegment [constr] StartX=5.75948 StartY=10 StartZ=0 EndX=-24.2405 EndY=10 EndZ=0
    g12: LineSegment StartX=-39.2405 StartY=65 StartZ=0 EndX=-29.2405 EndY=65 EndZ=0
    g13: LineSegment StartX=-29.2405 StartY=65 StartZ=0 EndX=0 EndY=65 EndZ=0
    g14: LineSegment StartX=31.54 StartY=0 StartZ=0 EndX=11.54 EndY=0 EndZ=0
    g15: Circle CenterX=-24.2405 CenterY=60 CenterZ=0 NormalX=0 NormalY=0 NormalZ=1 AngleXU=0 Radius=2
    g16: Circle CenterX=-9.24052 CenterY=60 CenterZ=0 NormalX=0 NormalY=0 NormalZ=1 AngleXU=0 Radius=2
    g17: LineSegment [constr] StartX=-24.2405 StartY=60 StartZ=0 EndX=-9.24052 EndY=60 EndZ=0
    g18: Circle CenterX=17.9917 CenterY=18.4952 CenterZ=0 NormalX=0 NormalY=0 NormalZ=1 AngleXU=0 Radius=2
    g19: Circle CenterX=24.54 CenterY=5 CenterZ=0 NormalX=0 NormalY=0 NormalZ=1 AngleXU=0 Radius=2
    g20: LineSegment [constr] StartX=17.9917 StartY=18.4952 StartZ=0 EndX=24.54 EndY=5 EndZ=0
    g21-g24: Circle [constr] x4 (B-spline internal-alignment scaffolding for g25; pole/knot coordinates omitted)
    g25: BSplineCurve PolesCount=4 KnotsCount=2 Degree=3 IsPeriodic=0
    g26: GeomPoint [constr] X=0 Y=65 Z=0
    g27: GeomPoint [constr] X=31.54 Y=0 Z=0
  constraints (60):
    c: PointOnObject(g0,g-1)
    c: Radius(g1) = 5
    c: Equal(g1,g2)
    c: Equal(g1,g3)
    c: Equal(g1,g4)
    c: Coincident(g5,g0)
    c: InternalAlignment(g1-g4 -> g5) x4
    c: InternalAlignment(g6,g5)
    c: InternalAlignment(g7,g5)
    c: Coincident(g8,g2)
    c: Vertical(g8)
    c: Coincident(g9,g2)
    c: Vertical(g9)
    c: Coincident(g10,g9)
    c: Coincident(g10,g3)
    c: Horizontal(g10)
    c: DistanceY(g8,g8) = 25
    c: DistanceY(g9,g9) = 30
    c: Coincident(g11,g0)
    c: Coincident(g11,g3)
    c: Horizontal(g11)
    c: DistanceX(g10,g10) = 15
    c: DistanceX(g11,g11) = 30
    c: DistanceX(g12,g12) = 10
    c: DistanceY(g0,g0) = 10
    c: DistanceX(g0,g0) = 11.54
    c: Coincident(g5,g8)
    c: Coincident(g5,g12)
    c: Horizontal(g12)
    c: Coincident(g13,g12)
    c: PointOnObject(g13,g-2)
    c: Horizontal(g13)
    c: Horizontal(g14)
    c: DistanceX(g14,g14) = 20
    c: Coincident(g14,g0)
    c: Radius(g15) = 2
    c: Radius(g16) = 2
    c: Coincident(g17,g15)
    c: Coincident(g17,g16)
    c: Horizontal(g17)
    c: DistanceY(g15,g5) = 5
    c: DistanceX(g5,g15) = 15
    c: DistanceX(g15,g16) = 15
    c: Radius(g18) = 2
    c: Equal(g18,g19) = 2
    c: Coincident(g20,g18)
    c: Coincident(g20,g19)
    c: DistanceY(g0,g19) = 5
    c: Coincident(g0,g-1)
    c: DistanceX(g0,g19) = 13
    c: Distance(g20) = 15
    c: Coincident(g25,g13)
    c: Radius(g21) = 6
    c: Equal(g21,g22)
    c: Equal(g21,g23)
    c: Equal(g21,g24)
    c: Coincident(g25,g14)
    c: InternalAlignment(g21-g24 -> g25) x4
    c: InternalAlignment(g26,g25)
    c: InternalAlignment(g27,g25)
FEATURE [Part::Extrusion] Extrude007  label="RBufferE"
  Base = -> Sketch015
  Dir = (0,0,1)
  DirMode = 2
  FaceMakerClass = Part::FaceMakerBullseye
  LengthFwd = 10
  LengthRev = 0
  Solid = true
  Symmetric = false
FEATURE [Sketcher::SketchObject] Sketch016  label="ResetbufferTop"
  MapMode = 5
  Placement = pos=(0,0,10) rot=(0,0,1;0rad)
  Support = -> [Extrude007]
  sketch-geometry (22):
    g0: ArcOfCircle CenterX=0 CenterY=0 CenterZ=0 NormalX=0 NormalY=0 NormalZ=1 AngleXU=0 Radius=11.54 StartAngle=0 EndAngle=1.04825
    g1-g4: Circle [constr] x4 (B-spline internal-alignment scaffolding for g5; pole/knot coordinates omitted)
    g5: BSplineCurve PolesCount=4 KnotsCount=2 Degree=3 IsPeriodic=0
    g6: GeomPoint [constr] X=-39.2405 Y=65 Z=0
    g7: GeomPoint [constr] X=5.75948 Y=10 Z=0
    g8: LineSegment [constr] StartX=-39.2405 StartY=65 StartZ=0 EndX=-39.2405 EndY=40 EndZ=0
    g9: LineSegment [constr] StartX=-39.2405 StartY=40 StartZ=0 EndX=-39.2405 EndY=10 EndZ=0
    g10: LineSegment [constr] StartX=-39.2405 StartY=10 StartZ=0 EndX=-24.2405 EndY=10 EndZ=0
    g11: LineSegment [constr] StartX=5.75948 StartY=10 StartZ=0 EndX=-24.2405 EndY=10 EndZ=0
    g12: LineSegment StartX=-39.2405 StartY=65 StartZ=0 EndX=-31.2405 EndY=65 EndZ=0
    g13: LineSegment StartX=16.54 StartY=0 StartZ=0 EndX=11.54 EndY=0 EndZ=0
    g14: ArcOfCircle CenterX=0 CenterY=0 CenterZ=0 NormalX=0 NormalY=0 NormalZ=1 AngleXU=0 Radius=16.54 StartAngle=0 EndAngle=1.5708
    g15-g18: Circle [constr] x4 (B-spline internal-alignment scaffolding for g19; pole/knot coordinates omitted)
    g19: BSplineCurve PolesCount=4 KnotsCount=2 Degree=3 IsPeriodic=0
    g20: GeomPoint [constr] X=1e-15 Y=16.54 Z=0
    g21: GeomPoint [constr] X=-31.2405 Y=65 Z=0
  constraints (47):
    c: PointOnObject(g0,g-1)
    c: Radius(g1) = 5
    c: Equal(g1,g2)
    c: Equal(g1,g3)
    c: Equal(g1,g4)
    c: Coincident(g5,g0)
    c: InternalAlignment(g1-g4 -> g5) x4
    c: InternalAlignment(g6,g5)
    c: InternalAlignment(g7,g5)
    c: Coincident(g8,g2)
    c: Vertical(g8)
    c: Coincident(g9,g2)
    c: Vertical(g9)
    c: Coincident(g10,g9)
    c: Coincident(g10,g3)
    c: Horizontal(g10)
    c: DistanceY(g8,g8) = 25
    c: DistanceY(g9,g9) = 30
    c: Coincident(g11,g0)
    c: Coincident(g11,g3)
    c: Horizontal(g11)
    c: DistanceX(g10,g10) = 15
    c: DistanceX(g11,g11) = 30
    c: DistanceX(g12,g12) = 8
    c: DistanceY(g0,g0) = 10
    c: DistanceX(g0,g0) = 11.54
    c: Coincident(g5,g8)
    c: Coincident(g5,g12)
    c: Horizontal(g12)
    c: Horizontal(g13)
    c: DistanceX(g13,g13) = 5
    c: Coincident(g13,g0)
    c: Coincident(g0,g-1)
    c: Coincident(g14,g0)
    c: Coincident(g14,g13)
    c: Coincident(g19,g14)
    c: Radius(g15) = 2
    c: Equal(g15,g16)
    c: Equal(g15,g17)
    c: Equal(g15,g18)
    c: Coincident(g19,g12)
    c: InternalAlignment(g15-g18 -> g19) x4
    c: InternalAlignment(g20,g19)
    c: InternalAlignment(g21,g19)
    c: DistanceX(g2,g17) = 10
    c: PointOnObject(g14,g-2)
    c: Distance(g16,g3) = 10
FEATURE [Sketcher::SketchObject] Sketch017  label="ResetbufferTop001"
  AttachmentOffset = pos=(-8,0,30) rot=(0,0,1;0rad)
  MapMode = 5
  Placement = pos=(-8,0,40) rot=(0,0,1;0rad)
  Support = -> [Extrude007]
  sketch-geometry (22):
    g0: ArcOfCircle CenterX=0 CenterY=0 CenterZ=0 NormalX=0 NormalY=0 NormalZ=1 AngleXU=0 Radius=11.54 StartAngle=0 EndAngle=1.04825
    g1-g4: Circle [constr] x4 (B-spline internal-alignment scaffolding for g5; pole/knot coordinates omitted)
    g5: BSplineCurve PolesCount=4 KnotsCount=2 Degree=3 IsPeriodic=0
    g6: GeomPoint [constr] X=-39.2405 Y=65 Z=0
    g7: GeomPoint [constr] X=5.75948 Y=10 Z=0
    g8: LineSegment [constr] StartX=-39.2405 StartY=65 StartZ=0 EndX=-39.2405 EndY=40 EndZ=0
    g9: LineSegment [constr] StartX=-39.2405 StartY=40 StartZ=0 EndX=-39.2405 EndY=10 EndZ=0
    g10: LineSegment [constr] StartX=-39.2405 StartY=10 StartZ=0 EndX=-24.2405 EndY=10 EndZ=0
    g11: LineSegment [constr] StartX=5.75948 StartY=10 StartZ=0 EndX=-24.2405 EndY=10 EndZ=0
    g12: LineSegment StartX=-39.2405 StartY=65 StartZ=0 EndX=-31.2405 EndY=65 EndZ=0
    g13: LineSegment StartX=16.54 StartY=0 StartZ=0 EndX=11.54 EndY=0 EndZ=0
    g14: ArcOfCircle CenterX=0 CenterY=0 CenterZ=0 NormalX=0 NormalY=0 NormalZ=1 AngleXU=0 Radius=16.54 StartAngle=0 EndAngle=1.5708
    g15-g18: Circle [constr] x4 (B-spline internal-alignment scaffolding for g19; pole/knot coordinates omitted)
    g19: BSplineCurve PolesCount=4 KnotsCount=2 Degree=3 IsPeriodic=0
    g20: GeomPoint [constr] X=1e-15 Y=16.54 Z=0
    g21: GeomPoint [constr] X=-31.2405 Y=65 Z=0
  constraints (47):
    c: PointOnObject(g0,g-1)
    c: Radius(g1) = 5
    c: Equal(g1,g2)
    c: Equal(g1,g3)
    c: Equal(g1,g4)
    c: Coincident(g5,g0)
    c: InternalAlignment(g1-g4 -> g5) x4
    c: InternalAlignment(g6,g5)
    c: InternalAlignment(g7,g5)
    c: Coincident(g8,g2)
    c: Vertical(g8)
    c: Coincident(g9,g2)
    c: Vertical(g9)
    c: Coincident(g10,g9)
    c: Coincident(g10,g3)
    c: Horizontal(g10)
    c: DistanceY(g8,g8) = 25
    c: DistanceY(g9,g9) = 30
    c: Coincident(g11,g0)
    c: Coincident(g11,g3)
    c: Horizontal(g11)
    c: DistanceX(g10,g10) = 15
    c: DistanceX(g11,g11) = 30
    c: DistanceX(g12,g12) = 8
    c: DistanceY(g0,g0) = 10
    c: DistanceX(g0,g0) = 11.54
    c: Coincident(g5,g8)
    c: Coincident(g5,g12)
    c: Horizontal(g12)
    c: Horizontal(g13)
    c: DistanceX(g13,g13) = 5
    c: Coincident(g13,g0)
    c: Coincident(g0,g-1)
    c: Coincident(g14,g0)
    c: Coincident(g14,g13)
    c: Coincident(g19,g14)
    c: Radius(g15) = 2
    c: Equal(g15,g16)
    c: Equal(g15,g17)
    c: Equal(g15,g18)
    c: Coincident(g19,g12)
    c: InternalAlignment(g15-g18 -> g19) x4
    c: InternalAlignment(g20,g19)
    c: InternalAlignment(g21,g19)
    c: DistanceX(g2,g17) = 10
    c: PointOnObject(g14,g-2)
    c: Distance(g16,g3) = 10
FEATURE [Part::Loft] Loft
  Closed = false
  MaxDegree = 5
  Ruled = false
  Sections = -> [Sketch016,Sketch017]
  Solid = true
FEATURE [Part::MultiFuse] Fusion005
  Shapes = -> [Extrude007,Loft]
FEATURE [Part::Mirroring] Part__Mirroring003  label="Fusion005 (Mirror #3)"
  Base = (0,0,0)
  Normal = (0,1,0)
  Source = -> Fusion005
FEATURE [Sketcher::SketchObject] Sketch019  label="RopeWhole"
  MapMode = 45
  Placement = pos=(5.55375,0,25) rot=(0.517869,0.517869,0.680899;1.94601rad)
  Support = -> [Part__Mirroring003,Fusion005]
  sketch-geometry (2):
    g0: Circle CenterX=0 CenterY=-15 CenterZ=0 NormalX=0 NormalY=0 NormalZ=1 AngleXU=0 Radius=4
    g1: Circle CenterX=0 CenterY=5 CenterZ=0 NormalX=0 NormalY=0 NormalZ=1 AngleXU=0 Radius=4
  constraints (6):
    c: PointOnObject(g0,g-2)
    c: Radius(g0) = 4
    c: DistanceY(g0) = -15
    c: PointOnObject(g1,g-2)
    c: Radius(g1) = 4
    c: DistanceY(g1) = 5
FEATURE [Part::MultiFuse] Fusion006  label="ResetBracket"
  Shapes = -> [Part__Mirroring003,Fusion005]
FEATURE [PartDesign::FeatureBase] BaseFeature
  BaseFeature = -> Fusion006
FEATURE [PartDesign::Pocket] Pocket005
  BaseFeature = -> BaseFeature
  Length = 10
  Length2 = 100
  Profile = -> Sketch019
  Reversed = true
  Type = 0
FEATURE [PartDesign::Body] Body
  BaseFeature = -> Fusion006
  Group = -> [BaseFeature,Sketch019,Pocket005]
  Origin = -> Origin
  Tip = -> Pocket005
FEATURE [TechDraw::DrawViewDimension] Dimension009
  Arbitrary = false
  FormatSpec = %.2f
  LockPosition = false
  MeasureType = 1
  OverTolerance = 0
  References2D = -> [View]
  Rotation = 0
  ScaleType = 0
  Type = 2
  UnderTolerance = 0
  X = -19.9903
  Y = -17.7705
FEATURE [TechDraw::DrawViewDimension] Dimension011
  Arbitrary = false
  FormatSpec = %.2f
  LockPosition = false
  MeasureType = 1
  OverTolerance = 0
  References2D = -> [View]
  Rotation = 0
  ScaleType = 0
  Type = 2
  UnderTolerance = 0
  X = 24.1972
  Y = -10.3784
FEATURE [TechDraw::DrawViewDimension] Dimension012
  Arbitrary = false
  FormatSpec = %.2f
  LockPosition = false
  MeasureType = 1
  OverTolerance = 0
  References2D = -> [View]
  Rotation = 0
  ScaleType = 0
  Type = 1
  UnderTolerance = 0
  X = 2.90055
  Y = -6.03153
FEATURE [TechDraw::DrawViewDimension] Dimension013
  Arbitrary = false
  FormatSpec = %.2f
  LockPosition = false
  MeasureType = 1
  OverTolerance = 0
  References2D = -> [View001]
  Rotation = 0
  ScaleType = 0
  Type = 2
  UnderTolerance = 0
  X = 30.002
  Y = 6.16637
FEATURE [TechDraw::DrawViewDimension] Dimension014
  Arbitrary = false
  FormatSpec = %.2f
  LockPosition = false
  MeasureType = 1
  OverTolerance = 0
  References2D = -> [View001]
  Rotation = 0
  ScaleType = 0
  Type = 1
  UnderTolerance = 0
  X = -5.82639
  Y = 16.1945
FEATURE [TechDraw::DrawViewAnnotation] Annotation
  Font = osifont
  LineSpace = 80
  LockPosition = false
  MaxWidth = -1
  Rotation = 0
  ScaleType = 0
  Text = NUI Galway
  TextSize = 5
  TextStyle = 2
  X = 202.343
  Y = 34.6454
FEATURE [TechDraw::DrawViewAnnotation] Annotation001
  Font = osifont
  LineSpace = 80
  LockPosition = false
  MaxWidth = -1
  Rotation = 0
  ScaleType = 0
  Text = NUI Galway
  TextSize = 5
  TextStyle = 2
  X = 202.343
  Y = 34.6454
FEATURE [TechDraw::DrawViewPart] View003  label=" Top"
  CoarseView = false
  Direction = (0,0,1)
  Focus = 100
  HardHidden = false
  IsoCount = 0
  IsoHidden = false
  IsoVisible = true
  LockPosition = false
  Perspective = false
  Rotation = 0
  Scale = 0.6
  ScaleType = 1
  SeamHidden = false
  SeamVisible = false
  SmoothHidden = false
  SmoothVisible = true
  Source = -> [Fusion006]
  X = 214.819
  Y = 130.373
FEATURE [TechDraw::DrawViewPart] View004  label=" Front"
  CoarseView = false
  Direction = (0,1,0)
  Focus = 100
  HardHidden = true
  IsoCount = 0
  IsoHidden = false
  IsoVisible = true
  LockPosition = false
  Perspective = true
  Rotation = 0
  Scale = 0.6
  ScaleType = 0
  SeamHidden = true
  SeamVisible = true
  SmoothHidden = true
  SmoothVisible = true
  Source = -> [Fusion006]
  X = 55.5596
  Y = 44.1451
FEATURE [TechDraw::DrawSVGTemplate] Template001
  EditableTexts = Designed_by_Name=Johannes Löwe; Drawing_number=0.0.1; FC-Date=08.08.2021; FC-SC=-; FC-SH=1; FC-Title=RWML Crawler; Subtitle=Reset Bracket; Weight=19.5 g
  Height = 210
  Orientation = 1
  Width = 297
FEATURE [TechDraw::DrawViewPart] View005  label=" Perspective"
  CoarseView = true
  Direction = (-0.2,1,1)
  Focus = 200
  HardHidden = false
  IsoCount = 0
  IsoHidden = false
  IsoVisible = true
  LockPosition = false
  Perspective = false
  Rotation = 0
  Scale = 0.75
  ScaleType = 0
  SeamHidden = false
  SeamVisible = false
  SmoothHidden = true
  SmoothVisible = false
  Source = -> [Fusion006]
  X = 55.6499
  Y = 151.083
  expr: Direction.x = -0.2
FEATURE [TechDraw::DrawViewDimension] Dimension
  Arbitrary = false
  FormatSpec = %.2f
  LockPosition = false
  MeasureType = 1
  OverTolerance = 0
  References2D = -> [View003]
  Rotation = 0
  ScaleType = 0
  Type = 2
  UnderTolerance = 0
  X = -47.3363
  Y = 0.276163
FEATURE [TechDraw::DrawViewDimension] Dimension015
  Arbitrary = false
  FormatSpec = %.2f
  LockPosition = false
  MeasureType = 1
  OverTolerance = 0
  References2D = -> [View003]
  Rotation = 0
  ScaleType = 0
  Type = 1
  UnderTolerance = 0
  X = -10.4191
  Y = 51.2704
FEATURE [TechDraw::DrawViewDimension] Dimension016
  Arbitrary = false
  FormatSpec = %.2f
  LockPosition = false
  MeasureType = 1
  OverTolerance = 0
  References2D = -> [View003]
  Rotation = 0
  ScaleType = 0
  Type = 1
  UnderTolerance = 0
  X = 3.46588
  Y = -50.429
FEATURE [TechDraw::DrawViewDimension] Dimension017
  Arbitrary = false
  FormatSpec = ⌀%.2f
  LockPosition = false
  MeasureType = 1
  OverTolerance = 0
  References2D = -> [View003]
  Rotation = 0
  ScaleType = 0
  Type = 5
  UnderTolerance = 0
  X = -16.4256
  Y = -46.3911
FEATURE [TechDraw::DrawViewDimension] Dimension018
  Arbitrary = false
  FormatSpec = %.2f
  LockPosition = false
  MeasureType = 1
  OverTolerance = 0
  References2D = -> [View003]
  Rotation = 0
  ScaleType = 0
  Type = 2
  UnderTolerance = 0
  X = -39.7759
  Y = 0.665901
FEATURE [TechDraw::DrawViewDimension] Dimension019
  Arbitrary = false
  FormatSpec = %.2f
  LockPosition = false
  MeasureType = 1
  OverTolerance = 0
  References2D = -> [View003]
  Rotation = 0
  ScaleType = 0
  Type = 1
  UnderTolerance = 0
  X = 11.1889
  Y = -27.7428
FEATURE [TechDraw::DrawViewDimension] Dimension020
  Arbitrary = false
  FormatSpec = %.2f
  LockPosition = false
  MeasureType = 1
  OverTolerance = 0
  References2D = -> [View003]
  Rotation = 0
  ScaleType = 0
  Type = 2
  UnderTolerance = 0
  X = 27.0093
  Y = -12.2792
FEATURE [TechDraw::DrawViewDimension] Dimension021
  Arbitrary = false
  FormatSpec = %.2f
  LockPosition = false
  MeasureType = 1
  OverTolerance = 0
  References2D = -> [View003]
  Rotation = 0
  ScaleType = 0
  Type = 0
  UnderTolerance = 0
  X = 0.243254
  Y = -16.5315
FEATURE [TechDraw::DrawViewDimension] Dimension022
  Arbitrary = false
  FormatSpec = %.2f
  LockPosition = false
  MeasureType = 1
  OverTolerance = 0
  References2D = -> [View004]
  Rotation = 0
  ScaleType = 0
  Type = 2
  UnderTolerance = 0
  X = 36.5997
  Y = -29.46
FEATURE [TechDraw::DrawViewDimension] Dimension023
  Arbitrary = false
  FormatSpec = %.2f
  LockPosition = false
  MeasureType = 1
  OverTolerance = 0
  References2D = -> [View004]
  Rotation = 0
  ScaleType = 0
  Type = 1
  UnderTolerance = 0
  X = 64.4126
  Y = 17.8147
FEATURE [TechDraw::DrawViewDimension] Dimension024
  Arbitrary = false
  FormatSpec = %.2f
  LockPosition = false
  MeasureType = 1
  OverTolerance = 0
  References2D = -> [View004]
  Rotation = 0
  ScaleType = 0
  Type = 2
  UnderTolerance = 0
  X = 44.3156
  Y = 5.54828
FEATURE [TechDraw::DrawViewDimension] Dimension025
  Arbitrary = false
  FormatSpec = %.2f
  LockPosition = false
  MeasureType = 1
  OverTolerance = 0
  References2D = -> [View004]
  Rotation = 0
  ScaleType = 0
  Type = 1
  UnderTolerance = 0
  X = 55.6251
  Y = 26.85
FEATURE [TechDraw::DrawViewDimension] Dimension026
  Arbitrary = false
  FormatSpec = %.2f
  LockPosition = false
  MeasureType = 1
  OverTolerance = 0
  References2D = -> [View004]
  Rotation = 0
  ScaleType = 0
  Type = 1
  UnderTolerance = 0
  X = 63.7221
  Y = -11.8161
FEATURE [TechDraw::DrawViewDimension] Dimension027
  Arbitrary = false
  FormatSpec = %.2f
  LockPosition = false
  MeasureType = 1
  OverTolerance = 0
  References2D = -> [View004]
  Rotation = 0
  ScaleType = 0
  Type = 1
  UnderTolerance = 0
  X = -17.0684
  Y = -19.1198
FEATURE [TechDraw::DrawViewDimension] Dimension028
  Arbitrary = false
  FormatSpec = %.2f
  LockPosition = false
  MeasureType = 1
  OverTolerance = 0
  References2D = -> [View004]
  Rotation = 0
  ScaleType = 0
  Type = 2
  UnderTolerance = 0
  X = -34.296
  Y = 1.22236
FEATURE [TechDraw::DrawPage] Page001
  KeepUpdated = true
  ProjectionType = 0
  Template = -> Template001
  Views = -> [View003,View004,View005,Annotation001,Dimension013,Dimension014,Dimension,Dimension015,Dimension016,Dimension017,Dimension018,Dimension019,Dimension020,Dimension021,Dimension022,Dimension023,Dimension024,Dimension025,Dimension026,Dimension027,Dimension028]
FEATURE [TechDraw::DrawViewDimension] Dimension029
  Arbitrary = false
  FormatSpec = %.2f
  LockPosition = false
  MeasureType = 1
  OverTolerance = 0
  References2D = -> [View]
  Rotation = 0
  ScaleType = 0
  Type = 2
  UnderTolerance = 0
  X = -54.5449
  Y = -1.11871
FEATURE [TechDraw::DrawViewDimension] Dimension030
  Arbitrary = false
  FormatSpec = %.2f
  LockPosition = false
  MeasureType = 1
  OverTolerance = 0
  References2D = -> [View]
  Rotation = 0
  ScaleType = 0
  Type = 1
  UnderTolerance = 0
  X = 4.40755
  Y = 19.8824
FEATURE [TechDraw::DrawViewDimension] Dimension031
  Arbitrary = false
  FormatSpec = %.2f
  LockPosition = false
  MeasureType = 1
  OverTolerance = 0
  References2D = -> [View]
  Rotation = 0
  ScaleType = 0
  Type = 1
  UnderTolerance = 0
  X = 19.958
  Y = -47.7499
FEATURE [TechDraw::DrawViewDimension] Dimension032
  Arbitrary = false
  FormatSpec = ⌀%.2f
  LockPosition = false
  MeasureType = 1
  OverTolerance = 0
  References2D = -> [View]
  Rotation = 0
  ScaleType = 0
  Type = 5
  UnderTolerance = 0
  X = 5.0679
  Y = 33.1325
FEATURE [TechDraw::DrawViewDimension] Dimension033
  Arbitrary = false
  FormatSpec = %.2f
  LockPosition = false
  MeasureType = 1
  OverTolerance = 0
  References2D = -> [View]
  Rotation = 0
  ScaleType = 0
  Type = 2
  UnderTolerance = 0
  X = -19.9808
  Y = 21.4607
FEATURE [TechDraw::DrawPage] Page
  KeepUpdated = true
  ProjectionType = 0
  Template = -> Template
  Views = -> [View,View001,View002,Annotation,Dimension009,Dimension011,Dimension012,Dimension013,Dimension014,Dimension029,Dimension030,Dimension031,Dimension032,Dimension033]
